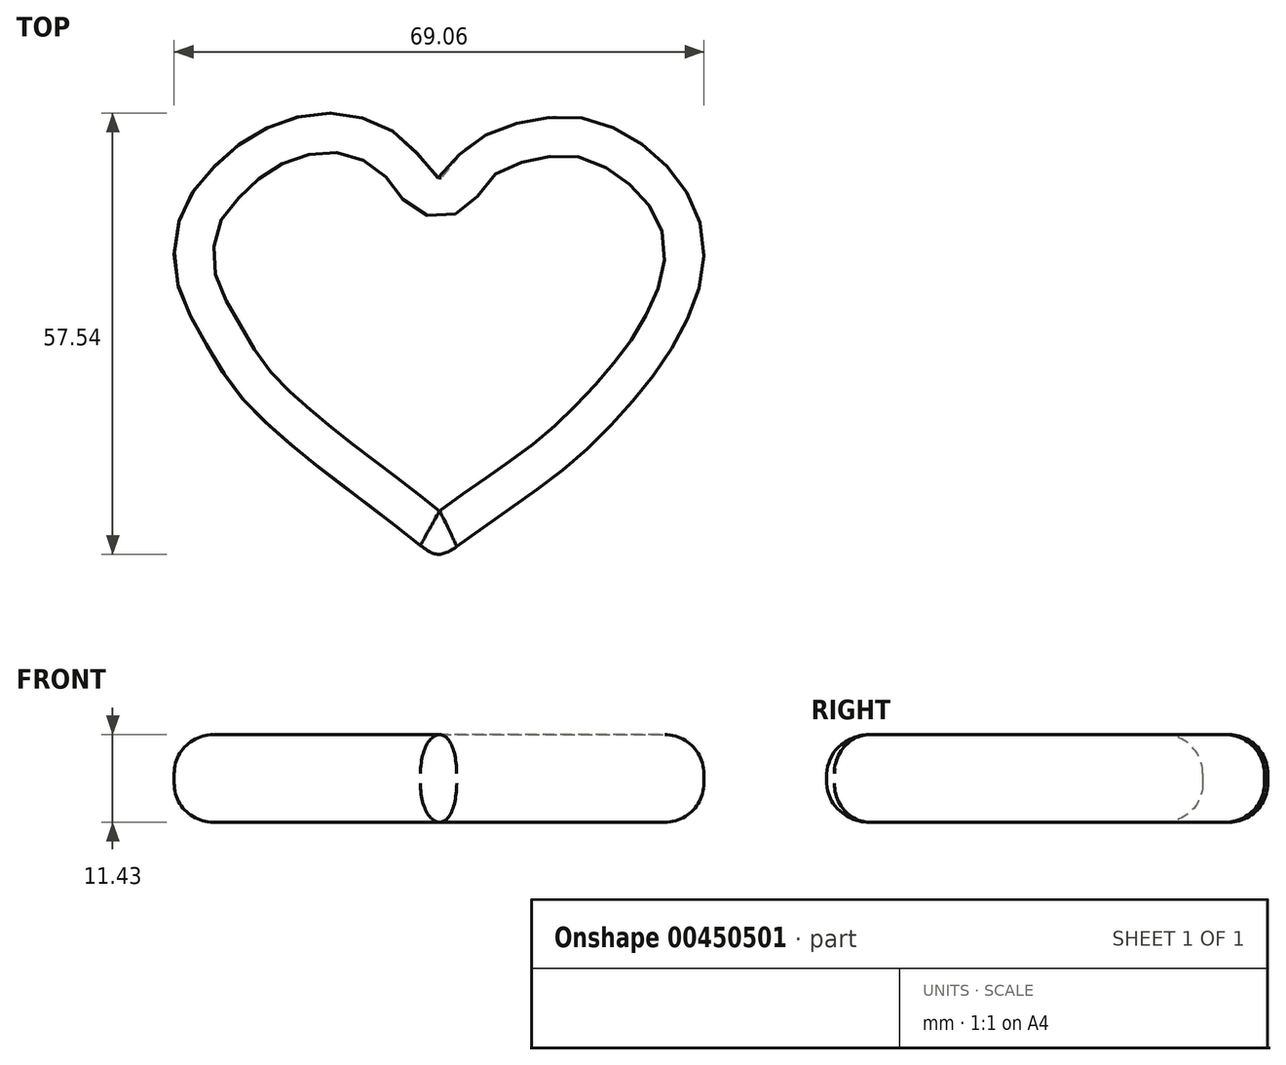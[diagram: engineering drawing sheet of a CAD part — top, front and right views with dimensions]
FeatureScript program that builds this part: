
annotation { "Feature Type Name" : "Feature", "Feature Type Description" : "" }
export const myFeature = defineFeature(function(context is Context, id is Id, definition is map)
    precondition{}
    {
        {
            var Q0;
            Q0=qCreatedBy(makeId("Top.planeOp"),FACE);
            var sketch = newSketch(context, id + "F0", { "sketchPlane" : qUnion([Q0])});
            skFitSpline(sketch, "E0", {"points": [v(0, 21.94) * mm, v(-3.46, 25.85) * mm, v(-7.5, 28.79) * mm, v(-13.62, 30.41) * mm, v(-21.57, 28.92) * mm, v(-27.23, 25.41) * mm, v(-31.93, 20.46) * mm, v(-33.88, 16.55) * mm, v(-34.53, 10.42) * mm, v(-32.97, 4.95) * mm, v(-30.23, 0) * mm, v(-26.71, -5.6) * mm, v(-23.59, -9) * mm, v(-17.98, -13.94) * mm, v(-3.7, -24.98) * mm, v(0, -27.1) * mm, v(4.25, -24.65) * mm, v(15.38, -16.68) * mm, v(23.33, -9.25) * mm, v(30.5, 0) * mm, v(34.27, 9.64) * mm, v(33.75, 16.8) * mm, v(29.84, 23.33) * mm, v(22.54, 28.6) * mm, v(14.65, 29.9) * mm, v(3.06, 25.53) * mm, v(0, 21.94) * mm]});
            skSolve(sketch);
        }
        {
            var Q0;
            Q0=makeQuery(id+"F0.imprint","IMPRINT",FACE,{"disambiguationData":[TD([[makeQuery(id+"F0.imprint","IMPRINT",EDGE,{"derivedFrom":sQuery(id+"F0.wireOp",EDGE,"E0")}),1.0]])]});
            extrude(context, id + "F1", {"entities" : qUnion([Q0]), "depth" : 11.43 * mm});
        }
        {
            var Q0;
            Q0=makeQuery(id+"F1.opExtrude","CAP_EDGE",EDGE,{"disambiguationData":[OSD([sQuery(id+"F0.wireOp",EDGE,"E0")])],"isStart":false});
            var Q1;
            Q1=makeQuery(id+"F1.opExtrude","CAP_EDGE",EDGE,{"disambiguationData":[OSD([sQuery(id+"F0.wireOp",EDGE,"E0")])],"isStart":true});
            fillet(context, id + "F2", {"entities" : qUnion([Q0, Q1]), "radius" : 5.08 * mm, "tangentPropagation" : true, "allowEdgeOverflow" : false});
        }
    });
